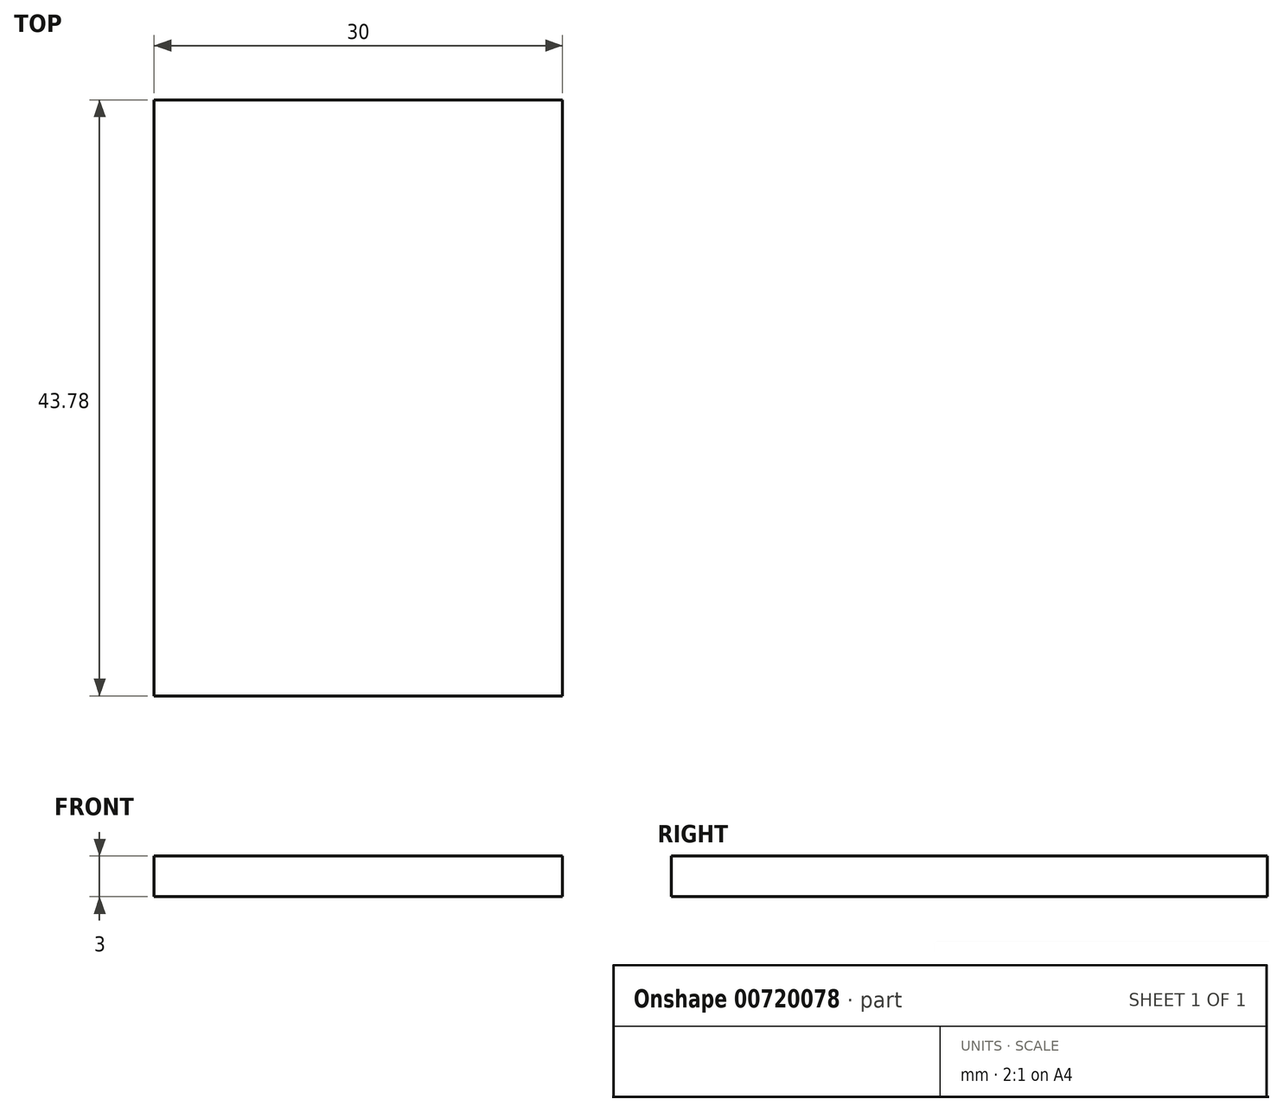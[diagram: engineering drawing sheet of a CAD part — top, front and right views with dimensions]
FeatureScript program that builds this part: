
annotation { "Feature Type Name" : "Feature", "Feature Type Description" : "" }
export const myFeature = defineFeature(function(context is Context, id is Id, definition is map)
    precondition{}
    {
        {
            var Q0;
            Q0=qCreatedBy(makeId("Top.planeOp"),FACE);
            var sketch = newSketch(context, id + "F0", { "sketchPlane" : qUnion([Q0])});
            skLineSegment(sketch, "E0.bottom", {"start": v(0, 0) * mm, "end": v(30, 0) * mm});
            skLineSegment(sketch, "E0.top", {"start": v(0, 43.78) * mm, "end": v(30, 43.78) * mm});
            skLineSegment(sketch, "E0.left", {"start": v(0, 0) * mm, "end": v(0, 43.78) * mm});
            skLineSegment(sketch, "E0.right", {"start": v(30, 0) * mm, "end": v(30, 43.78) * mm});
            skSolve(sketch);
        }
        {
            var Q0;
            Q0=makeQuery(id+"F0.imprint","IMPRINT",FACE,{"disambiguationData":[TD([[makeQuery(id+"F0.imprint","IMPRINT",EDGE,{"derivedFrom":sQuery(id+"F0.wireOp",EDGE,"E0.bottom")}),1.0]])]});
            extrude(context, id + "F1", {"entities" : qUnion([Q0]), "depth" : 3 * mm, "offsetDistance" : 25 * mm});
        }
    });
